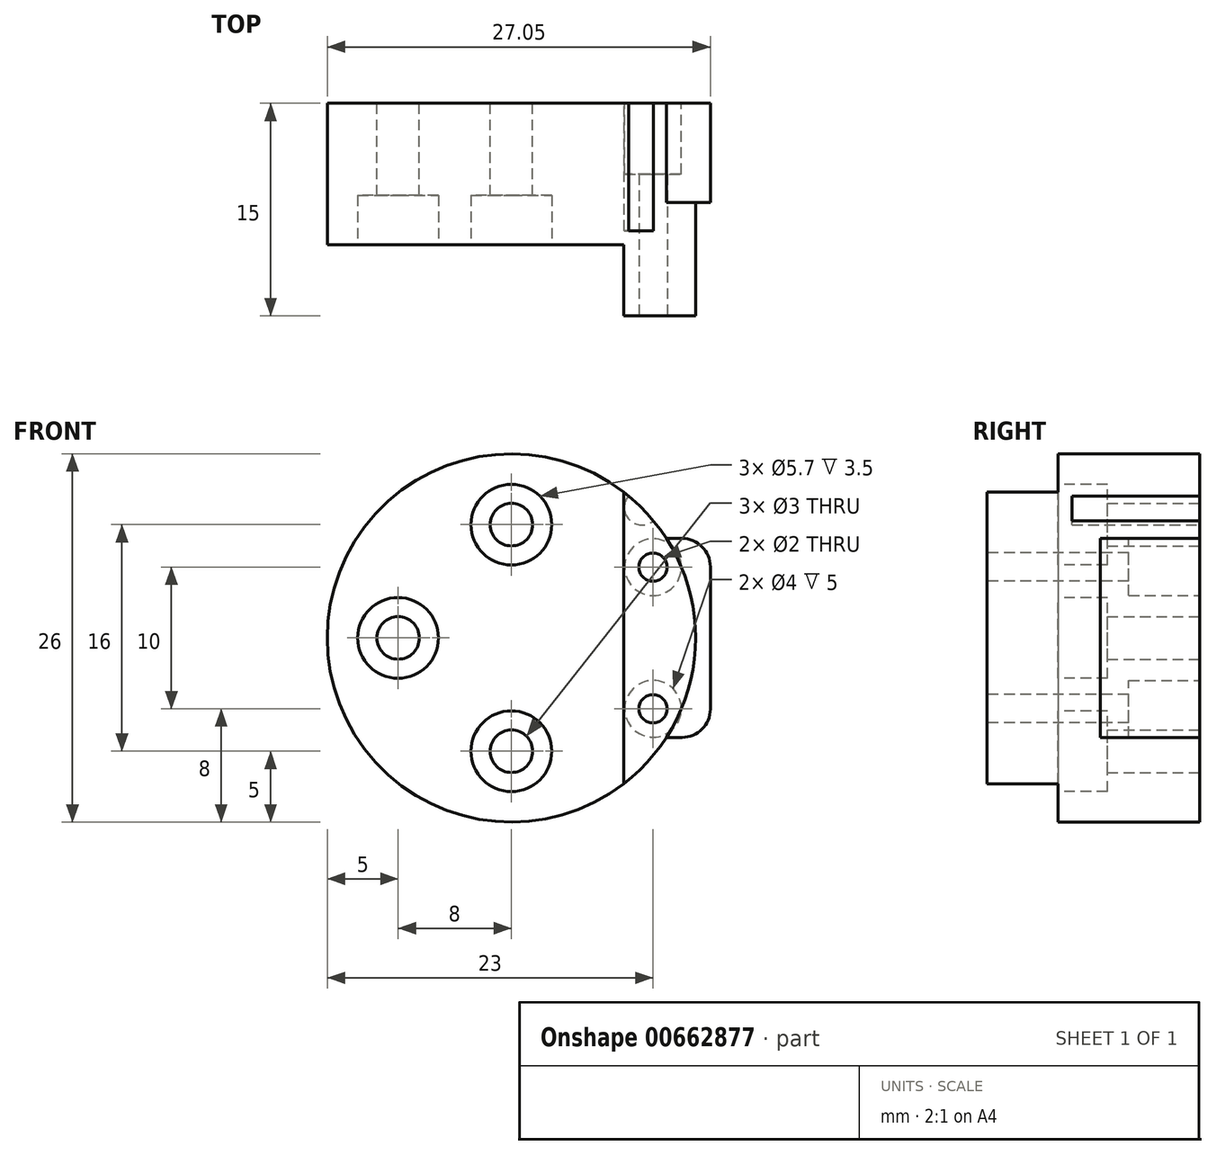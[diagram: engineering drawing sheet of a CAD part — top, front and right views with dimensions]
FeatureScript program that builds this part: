
annotation { "Feature Type Name" : "Feature", "Feature Type Description" : "" }
export const myFeature = defineFeature(function(context is Context, id is Id, definition is map)
    precondition{}
    {
        {
            var Q0;
            Q0=qCreatedBy(makeId("Front.planeOp"),FACE);
            var sketch = newSketch(context, id + "F0", { "sketchPlane" : qUnion([Q0])});
            skCircle(sketch, "E0", {"center": v(0, 0) * mm, "radius": 13 * mm});
            skCircle(sketch, "E1", {"center": v(-8, 0) * mm, "radius": 1.5 * mm});
            skCircle(sketch, "E2", {"center": v(0, 8) * mm, "radius": 1.5 * mm});
            skCircle(sketch, "E3.MirrorC", {"center": v(0, -8) * mm, "radius": 1.5 * mm});
            skLineSegment(sketch, "E4.bottom", {"start": v(10.94, 7.03) * mm, "end": v(14.05, 7.03) * mm});
            skLineSegment(sketch, "E4.top", {"start": v(10.94, -7.03) * mm, "end": v(14.05, -7.03) * mm});
            skLineSegment(sketch, "E4.left", {"start": v(10.94, 7.03) * mm, "end": v(10.94, -7.03) * mm});
            skLineSegment(sketch, "E4.right", {"start": v(14.05, 7.03) * mm, "end": v(14.05, -7.03) * mm});
            skSolve(sketch);
        }
        {
            var Q0;
            Q0 = qSketchRegion(id + "F0", true);
            extrude(context, id + "F1", {"entities" : qUnion([Q0]), "depth" : 15 * mm, "offsetDistance" : 25.4 * mm});
        }
        {
            var Q0;
            Q0=qCreatedBy(makeId("Front.planeOp"),FACE);
            var sketch = newSketch(context, id + "F2", { "sketchPlane" : qUnion([Q0])});
            skCircle(sketch, "E5", {"center": v(0, 0) * mm, "radius": 15.85 * mm});
            skSolve(sketch);
        }
        {
            var Q0;
            Q0=makeQuery(id+"F1.opExtrude","CAP_FACE",FACE,{"disambiguationData":[OSD([sQuery(id+"F0.wireOp",EDGE,"E0"),sQuery(id+"F0.wireOp",EDGE,"E1"),sQuery(id+"F0.wireOp",EDGE,"E2"),sQuery(id+"F0.wireOp",EDGE,"E3.MirrorC")])],"isStart":false});
            var sketch = newSketch(context, id + "F3", { "sketchPlane" : qUnion([Q0])});
            skLineSegment(sketch, "E6", {"start": v(10, 8.3) * mm, "end": v(10, -8.3) * mm});
            skCircle(sketch, "E7", {"center": v(10, 5) * mm, "radius": 1 * mm});
            skCircle(sketch, "E8.MirrorC", {"center": v(10, -5) * mm, "radius": 1 * mm});
            skSolve(sketch);
        }
        {
            var Q0;
            Q0 = qSketchRegion(id + "F3", true);
            var Q1;
            Q1=sQuery(id+"F3.wireOp",EDGE,"E8.MirrorC");
            var Q2;
            Q2=sQuery(id+"F3.wireOp",EDGE,"E7");
            extrude(context, id + "F4", {"entities" : qUnion([Q0]), "operationType" : NewBodyOperationType.REMOVE, "surfaceEntities" : qUnion([Q1, Q2]), "oppositeDirection" : true, "depth" : 15 * mm, "offsetDistance" : 25.4 * mm});
        }
        {
            var Q0;
            Q0=makeQuery(id+"F2.imprint","IMPRINT",FACE,{"disambiguationData":[TD([[makeQuery(id+"F2.imprint","IMPRINT",EDGE,{"derivedFrom":sQuery(id+"F2.wireOp",EDGE,"E5")}),1.0]])]});
            var sketch = newSketch(context, id + "F5", { "sketchPlane" : qUnion([Q0])});
            skCircle(sketch, "E9", {"center": v(10, 5) * mm, "radius": 2 * mm});
            skCircle(sketch, "E10.MirrorC", {"center": v(10, -5) * mm, "radius": 2 * mm});
            skSolve(sketch);
        }
        {
            var Q0;
            Q0 = qSketchRegion(id + "F5", true);
            extrude(context, id + "F6", {"entities" : qUnion([Q0]), "operationType" : NewBodyOperationType.REMOVE, "depth" : 5 * mm, "offsetDistance" : 25.4 * mm});
        }
        {
            var Q0;
            Q0=makeQuery(id+"F1.opExtrude","CAP_FACE",FACE,{"disambiguationData":[OSD([sQuery(id+"F0.wireOp",EDGE,"E0"),sQuery(id+"F0.wireOp",EDGE,"E1"),sQuery(id+"F0.wireOp",EDGE,"E2"),sQuery(id+"F0.wireOp",EDGE,"E3.MirrorC"),sQuery(id+"F0.wireOp",EDGE,"E4.bottom"),sQuery(id+"F0.wireOp",EDGE,"E4.top"),sQuery(id+"F0.wireOp",EDGE,"E4.right")])],"isStart":false});
            var sketch = newSketch(context, id + "F7", { "sketchPlane" : qUnion([Q0])});
            skCircle(sketch, "E11", {"center": v(0, 8) * mm, "radius": 2.85 * mm});
            skCircle(sketch, "E12.MirrorC", {"center": v(0, -8) * mm, "radius": 2.85 * mm});
            skCircle(sketch, "E13", {"center": v(-8, 0) * mm, "radius": 2.85 * mm});
            skSolve(sketch);
        }
        {
            var Q0;
            Q0 = qSketchRegion(id + "F7", true);
            extrude(context, id + "F8", {"entities" : qUnion([Q0]), "operationType" : NewBodyOperationType.REMOVE, "oppositeDirection" : true, "depth" : 8.5 * mm, "offsetDistance" : 25.4 * mm});
        }
        {
            var Q0;
            Q0=makeQuery(id+"F1.opExtrude","SWEPT_EDGE",EDGE,{"disambiguationData":[OSD([sQuery(id+"F0.wireOp",EDGE,"E4.bottom"),sQuery(id+"F0.wireOp",EDGE,"E4.right")])]});
            var Q1;
            Q1=makeQuery(id+"F1.opExtrude","SWEPT_EDGE",EDGE,{"disambiguationData":[OSD([sQuery(id+"F0.wireOp",EDGE,"E4.top"),sQuery(id+"F0.wireOp",EDGE,"E4.right")])]});
            fillet(context, id + "F9", {"entities" : qUnion([Q0, Q1]), "radius" : 2 * mm, "tangentPropagation" : true, "allowEdgeOverflow" : false});
        }
        {
            var Q0;
            Q0=makeQuery(id+"F2.imprint","IMPRINT",FACE,{"disambiguationData":[TD([[makeQuery(id+"F2.imprint","IMPRINT",EDGE,{"derivedFrom":sQuery(id+"F2.wireOp",EDGE,"E5")}),1.0]])]});
            var sketch = newSketch(context, id + "F10", { "sketchPlane" : qUnion([Q0])});
            skCircle(sketch, "E14", {"center": v(9.22, 9.22) * mm, "radius": 1.25 * mm});
            skSolve(sketch);
        }
        {
            var Q0;
            Q0 = qSketchRegion(id + "F10", true);
            extrude(context, id + "F11", {"entities" : qUnion([Q0]), "operationType" : NewBodyOperationType.REMOVE, "depth" : 9 * mm, "offsetDistance" : 25.4 * mm});
        }
        {
            var Q0;
            Q0=makeQuery(id+"F1.opExtrude","CAP_FACE",FACE,{"disambiguationData":[OSD([sQuery(id+"F0.wireOp",EDGE,"E0"),sQuery(id+"F0.wireOp",EDGE,"E1"),sQuery(id+"F0.wireOp",EDGE,"E2"),sQuery(id+"F0.wireOp",EDGE,"E3.MirrorC"),sQuery(id+"F0.wireOp",EDGE,"E4.bottom"),sQuery(id+"F0.wireOp",EDGE,"E4.top"),sQuery(id+"F0.wireOp",EDGE,"E4.right")])],"isStart":false});
            var sketch = newSketch(context, id + "F12", { "sketchPlane" : qUnion([Q0])});
            skPoint(sketch, "E15.middle", {"position": v(14.05, 0) * mm});
            skCircle(sketch, "E16", {"center": v(0, 0) * mm, "radius": 13 * mm});
            skLineSegment(sketch, "E17.bottom", {"start": v(10.94, 7.03) * mm, "end": v(14.05, 7.03) * mm});
            skLineSegment(sketch, "E17.top", {"start": v(10.94, -7.19) * mm, "end": v(14.05, -7.19) * mm});
            skLineSegment(sketch, "E17.left", {"start": v(10.94, 7.03) * mm, "end": v(10.94, -7.19) * mm});
            skLineSegment(sketch, "E17.right", {"start": v(14.05, 7.03) * mm, "end": v(14.05, -7.19) * mm});
            skSolve(sketch);
        }
        {
            var Q0;
            {var subQ1=sQuery(id+"F0.wireOp",EDGE,"E4.top");var subQ11=makeQuery(id+"F1.opExtrude","CAP_EDGE",EDGE,{"disambiguationData":[OSD([subQ1])],"isStart":false});Q0=makeQuery(id+"F12.imprint","IMPRINT",FACE,{"disambiguationData":[TD([[makeQuery(id+"F12.imprint","IMPRINT",EDGE,{"derivedFrom":subQ11}),1.0]])]});}
            extrude(context, id + "F13", {"entities" : qUnion([Q0]), "operationType" : NewBodyOperationType.REMOVE, "oppositeDirection" : true, "depth" : 8 * mm, "offsetDistance" : 25.4 * mm});
        }
        {
            var Q0;
            Q0=makeQuery(id+"F1.opExtrude","CAP_FACE",FACE,{"disambiguationData":[OSD([sQuery(id+"F0.wireOp",EDGE,"E0"),sQuery(id+"F0.wireOp",EDGE,"E1"),sQuery(id+"F0.wireOp",EDGE,"E2"),sQuery(id+"F0.wireOp",EDGE,"E3.MirrorC"),sQuery(id+"F0.wireOp",EDGE,"E4.bottom"),sQuery(id+"F0.wireOp",EDGE,"E4.top"),sQuery(id+"F0.wireOp",EDGE,"E4.right")])],"isStart":false});
            var sketch = newSketch(context, id + "F14", { "sketchPlane" : qUnion([Q0])});
            skCircle(sketch, "E18", {"center": v(0, 0) * mm, "radius": 13 * mm});
            skLineSegment(sketch, "E19", {"start": v(7.93, 10.3) * mm, "end": v(7.93, -10.3) * mm});
            skSolve(sketch);
        }
        {
            var Q0;
            {var subQ0=sQuery(id+"F14.wireOp",EDGE,"E19");Q0=makeQuery(id+"F14.imprint","IMPRINT",FACE,{"disambiguationData":[TD([[makeQuery(id+"F14.imprint","IMPRINT",EDGE,{"derivedFrom":subQ0}),-1.0]])]});}
            extrude(context, id + "F15", {"entities" : qUnion([Q0]), "operationType" : NewBodyOperationType.REMOVE, "oppositeDirection" : true, "depth" : 5 * mm, "offsetDistance" : 25.4 * mm});
        }
    });
